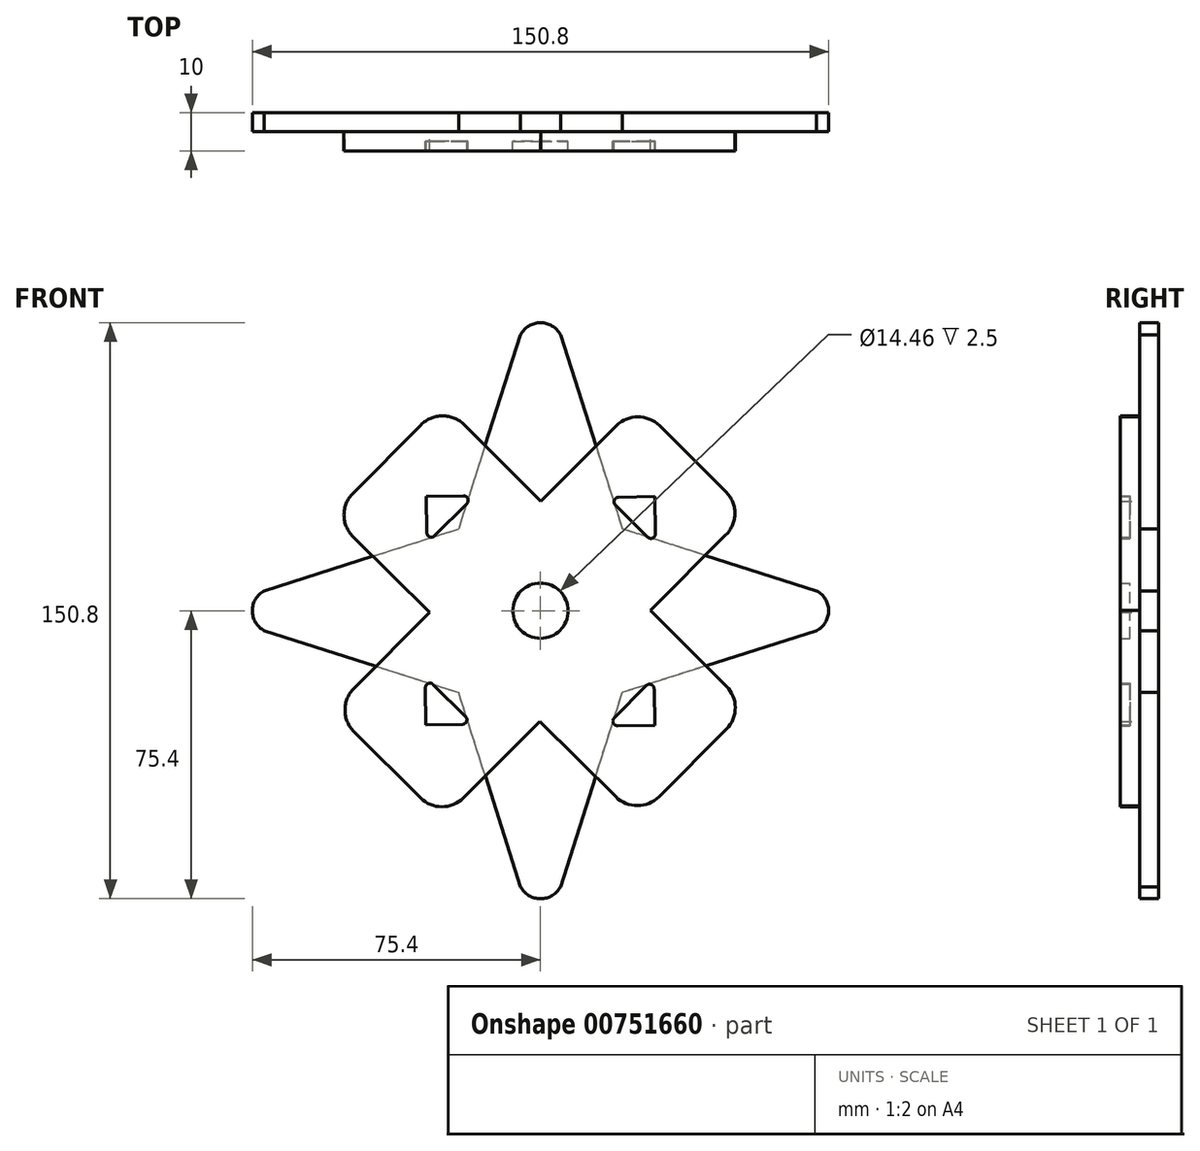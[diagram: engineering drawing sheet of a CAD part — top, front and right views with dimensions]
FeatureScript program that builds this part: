
annotation { "Feature Type Name" : "Feature", "Feature Type Description" : "" }
export const myFeature = defineFeature(function(context is Context, id is Id, definition is map)
    precondition{}
    {
        {
            var Q0;
            Q0=qCreatedBy(makeId("Front.planeOp"),FACE);
            var sketch = newSketch(context, id + "F0", { "sketchPlane" : qUnion([Q0])});
            skArc(sketch, "E0", {"start": v(5.71, 71.02) * mm, "mid": v(0.66, 75.37) * mm, "end": v(-5.23, 72.25) * mm});
            skLineSegment(sketch, "E1", {"start": v(-5.23, 72.25) * mm, "end": v(-21.41, 21.41) * mm});
            skLineSegment(sketch, "E2.MirrorCS", {"start": v(5.23, 72.25) * mm, "end": v(21.41, 21.41) * mm});
            skLineSegment(sketch, "E3", {"start": v(0, 75.37) * mm, "end": v(0, 0) * mm});
            skPoint(sketch, "E3.startSnap0", {"position": v(0.66, 75.37) * mm});
            skLineSegment(sketch, "E4.1.0", {"start": v(-75.37, 0) * mm, "end": v(0, 0) * mm});
            skArc(sketch, "E4.1.1", {"start": v(-71.02, 5.71) * mm, "mid": v(-75.37, 0.66) * mm, "end": v(-72.25, -5.23) * mm});
            skPoint(sketch, "E4.1.2", {"position": v(-75.37, 0.66) * mm});
            skLineSegment(sketch, "E4.1.3", {"start": v(-72.25, -5.23) * mm, "end": v(-21.41, -21.41) * mm});
            skLineSegment(sketch, "E4.1.4", {"start": v(-72.25, 5.23) * mm, "end": v(-21.41, 21.41) * mm});
            skLineSegment(sketch, "E4.2.0", {"start": v(0, -75.37) * mm, "end": v(0, 0) * mm});
            skArc(sketch, "E4.2.1", {"start": v(-5.71, -71.02) * mm, "mid": v(-0.66, -75.37) * mm, "end": v(5.23, -72.25) * mm});
            skPoint(sketch, "E4.2.2", {"position": v(-0.66, -75.37) * mm});
            skLineSegment(sketch, "E4.2.3", {"start": v(5.23, -72.25) * mm, "end": v(21.41, -21.41) * mm});
            skLineSegment(sketch, "E4.2.4", {"start": v(-5.23, -72.25) * mm, "end": v(-21.41, -21.41) * mm});
            skLineSegment(sketch, "E4.3.0", {"start": v(75.37, 0) * mm, "end": v(0, 0) * mm});
            skArc(sketch, "E4.3.1", {"start": v(71.02, -5.71) * mm, "mid": v(75.37, -0.66) * mm, "end": v(72.25, 5.23) * mm});
            skPoint(sketch, "E4.3.2", {"position": v(75.37, -0.66) * mm});
            skLineSegment(sketch, "E4.3.3", {"start": v(72.25, 5.23) * mm, "end": v(21.41, 21.41) * mm});
            skLineSegment(sketch, "E4.3.4", {"start": v(72.25, -5.23) * mm, "end": v(21.41, -21.41) * mm});
            skPoint(sketch, "E4.center", {"position": v(0, 0) * mm});
            skPoint(sketch, "E5.orphan", {"position": v(-18.17, 22.45) * mm});
            skPoint(sketch, "E6.orphan", {"position": v(-22.45, 18.17) * mm});
            skPoint(sketch, "E7.orphan", {"position": v(18.17, 22.45) * mm});
            skPoint(sketch, "E8.orphan", {"position": v(22.45, 18.17) * mm});
            skPoint(sketch, "E9.orphan", {"position": v(22.45, -18.17) * mm});
            skPoint(sketch, "E10.orphan", {"position": v(18.17, -22.45) * mm});
            skPoint(sketch, "E11.orphan", {"position": v(-18.17, -22.45) * mm});
            skPoint(sketch, "E12.orphan", {"position": v(-22.45, -18.17) * mm});
            skSolve(sketch);
        }
        {
            var Q0;
            Q0 = qSketchRegion(id + "F0", true);
            extrude(context, id + "F1", {"entities" : qUnion([Q0]), "oppositeDirection" : true, "depth" : 5 * mm, "offsetDistance" : 25 * mm});
        }
        {
            var Q0;
            Q0=qCreatedBy(makeId("Front.planeOp"),FACE);
            var sketch = newSketch(context, id + "F2", { "sketchPlane" : qUnion([Q0])});
            skLineSegment(sketch, "E13", {"start": v(-49.1, 30.74) * mm, "end": v(-31.28, 48.66) * mm});
            skLineSegment(sketch, "E14", {"start": v(-19.95, 48.69) * mm, "end": v(48.62, -19.7) * mm});
            skLineSegment(sketch, "E15", {"start": v(48.63, -31.01) * mm, "end": v(31, -48.68) * mm});
            skLineSegment(sketch, "E16", {"start": v(19.71, -48.72) * mm, "end": v(-49.05, 19.42) * mm});
            skPoint(sketch, "E17.visualSharp", {"position": v(-54.74, 25.05) * mm});
            skArc(sketch, "E17.filletArc", {"start": v(-49.1, 30.74) * mm, "mid": v(-51.42, 25.07) * mm, "end": v(-49.05, 19.42) * mm});
            skPoint(sketch, "E18.visualSharp", {"position": v(-25.63, 54.35) * mm});
            skArc(sketch, "E18.filletArc", {"start": v(-19.95, 48.69) * mm, "mid": v(-25.62, 51.02) * mm, "end": v(-31.28, 48.66) * mm});
            skPoint(sketch, "E19.visualSharp", {"position": v(25.38, -54.33) * mm});
            skArc(sketch, "E19.filletArc", {"start": v(19.71, -48.72) * mm, "mid": v(25.37, -51.04) * mm, "end": v(31, -48.68) * mm});
            skPoint(sketch, "E20.visualSharp", {"position": v(54.28, -25.35) * mm});
            skArc(sketch, "E20.filletArc", {"start": v(48.63, -31.01) * mm, "mid": v(50.97, -25.35) * mm, "end": v(48.62, -19.7) * mm});
            skLineSegment(sketch, "E21", {"start": v(31.15, 48.44) * mm, "end": v(48.5, 31.2) * mm});
            skLineSegment(sketch, "E22", {"start": v(48.53, 19.87) * mm, "end": v(-20.12, -48.96) * mm});
            skLineSegment(sketch, "E23", {"start": v(-31.43, -48.98) * mm, "end": v(-48.81, -31.64) * mm});
            skLineSegment(sketch, "E24", {"start": v(-48.82, -20.32) * mm, "end": v(19.85, 48.42) * mm});
            skPoint(sketch, "E25.visualSharp", {"position": v(25.49, 54.06) * mm});
            skArc(sketch, "E25.filletArc", {"start": v(31.15, 48.44) * mm, "mid": v(25.5, 50.76) * mm, "end": v(19.85, 48.42) * mm});
            skPoint(sketch, "E26.visualSharp", {"position": v(54.19, 25.55) * mm});
            skArc(sketch, "E26.filletArc", {"start": v(48.53, 19.87) * mm, "mid": v(50.86, 25.54) * mm, "end": v(48.5, 31.2) * mm});
            skPoint(sketch, "E27.visualSharp", {"position": v(-54.48, -25.99) * mm});
            skArc(sketch, "E27.filletArc", {"start": v(-48.82, -20.32) * mm, "mid": v(-51.16, -25.99) * mm, "end": v(-48.81, -31.64) * mm});
            skPoint(sketch, "E28.visualSharp", {"position": v(-25.77, -54.63) * mm});
            skArc(sketch, "E28.filletArc", {"start": v(-31.43, -48.98) * mm, "mid": v(-25.77, -51.31) * mm, "end": v(-20.12, -48.96) * mm});
            skSolve(sketch);
        }
        {
            var Q0;
            Q0 = qSketchRegion(id + "F2", true);
            extrude(context, id + "F3", {"entities" : qUnion([Q0]), "depth" : 5 * mm, "offsetDistance" : 25 * mm});
        }
        {
            var Q0;
            Q0=makeQuery(id+"F2.imprint","IMPRINT",FACE,{"disambiguationData":[TD([[makeQuery(id+"F2.imprint","IMPRINT",EDGE,{"derivedFrom":sQuery(id+"F2.wireOp",EDGE,"E21")}),-1.0]])]});
            var sketch = newSketch(context, id + "F4", { "sketchPlane" : qUnion([Q0])});
            skLineSegment(sketch, "E29", {"start": v(28.05, 19.28) * mm, "end": v(23.7, 23.62) * mm});
            skLineSegment(sketch, "E30", {"start": v(20.43, 29.73) * mm, "end": v(29.98, 29.94) * mm});
            skLineSegment(sketch, "E31", {"start": v(30.1, 20.15) * mm, "end": v(29.98, 29.94) * mm});
            skLineSegment(sketch, "E32", {"start": v(23.96, 23.36) * mm, "end": v(19.6, 27.68) * mm});
            skLineSegment(sketch, "E33", {"start": v(23.96, 23.36) * mm, "end": v(23.7, 23.62) * mm});
            skPoint(sketch, "E34.visualSharp", {"position": v(17.61, 29.67) * mm});
            skArc(sketch, "E34.filletArc", {"start": v(20.43, 29.73) * mm, "mid": v(19.34, 28.98) * mm, "end": v(19.6, 27.68) * mm});
            skPoint(sketch, "E35.visualSharp", {"position": v(30.13, 17.21) * mm});
            skArc(sketch, "E35.filletArc", {"start": v(28.05, 19.28) * mm, "mid": v(29.37, 19.03) * mm, "end": v(30.1, 20.15) * mm});
            skLineSegment(sketch, "E36.1.0", {"start": v(-23.36, 23.96) * mm, "end": v(-27.68, 19.6) * mm});
            skLineSegment(sketch, "E36.1.1", {"start": v(-20.15, 30.1) * mm, "end": v(-29.94, 29.98) * mm});
            skPoint(sketch, "E36.1.2", {"position": v(-17.21, 30.13) * mm});
            skLineSegment(sketch, "E36.1.3", {"start": v(-29.73, 20.43) * mm, "end": v(-29.94, 29.98) * mm});
            skPoint(sketch, "E36.1.4", {"position": v(-29.67, 17.61) * mm});
            skLineSegment(sketch, "E36.1.5", {"start": v(-19.28, 28.05) * mm, "end": v(-23.62, 23.7) * mm});
            skLineSegment(sketch, "E36.1.6", {"start": v(-23.36, 23.96) * mm, "end": v(-23.62, 23.7) * mm});
            skArc(sketch, "E36.1.7", {"start": v(-29.73, 20.43) * mm, "mid": v(-28.98, 19.34) * mm, "end": v(-27.68, 19.6) * mm});
            skArc(sketch, "E36.1.8", {"start": v(-19.28, 28.05) * mm, "mid": v(-19.03, 29.37) * mm, "end": v(-20.15, 30.1) * mm});
            skLineSegment(sketch, "E36.2.0", {"start": v(-23.96, -23.36) * mm, "end": v(-19.6, -27.68) * mm});
            skLineSegment(sketch, "E36.2.1", {"start": v(-30.1, -20.15) * mm, "end": v(-29.98, -29.94) * mm});
            skPoint(sketch, "E36.2.2", {"position": v(-30.13, -17.21) * mm});
            skLineSegment(sketch, "E36.2.3", {"start": v(-20.43, -29.73) * mm, "end": v(-29.98, -29.94) * mm});
            skPoint(sketch, "E36.2.4", {"position": v(-17.61, -29.67) * mm});
            skLineSegment(sketch, "E36.2.5", {"start": v(-28.05, -19.28) * mm, "end": v(-23.7, -23.62) * mm});
            skLineSegment(sketch, "E36.2.6", {"start": v(-23.96, -23.36) * mm, "end": v(-23.7, -23.62) * mm});
            skArc(sketch, "E36.2.7", {"start": v(-20.43, -29.73) * mm, "mid": v(-19.34, -28.98) * mm, "end": v(-19.6, -27.68) * mm});
            skArc(sketch, "E36.2.8", {"start": v(-28.05, -19.28) * mm, "mid": v(-29.37, -19.03) * mm, "end": v(-30.1, -20.15) * mm});
            skLineSegment(sketch, "E36.3.0", {"start": v(23.36, -23.96) * mm, "end": v(27.68, -19.6) * mm});
            skLineSegment(sketch, "E36.3.1", {"start": v(20.15, -30.1) * mm, "end": v(29.94, -29.98) * mm});
            skPoint(sketch, "E36.3.2", {"position": v(17.21, -30.13) * mm});
            skLineSegment(sketch, "E36.3.3", {"start": v(29.73, -20.43) * mm, "end": v(29.94, -29.98) * mm});
            skPoint(sketch, "E36.3.4", {"position": v(29.67, -17.61) * mm});
            skLineSegment(sketch, "E36.3.5", {"start": v(19.28, -28.05) * mm, "end": v(23.62, -23.7) * mm});
            skLineSegment(sketch, "E36.3.6", {"start": v(23.36, -23.96) * mm, "end": v(23.62, -23.7) * mm});
            skArc(sketch, "E36.3.7", {"start": v(29.73, -20.43) * mm, "mid": v(28.98, -19.34) * mm, "end": v(27.68, -19.6) * mm});
            skArc(sketch, "E36.3.8", {"start": v(19.28, -28.05) * mm, "mid": v(19.03, -29.37) * mm, "end": v(20.15, -30.1) * mm});
            skPoint(sketch, "E36.center", {"position": v(0, 0) * mm});
            skSolve(sketch);
        }
        {
            var Q0;
            Q0 = qSketchRegion(id + "F4", true);
            extrude(context, id + "F5", {"entities" : qUnion([Q0]), "operationType" : NewBodyOperationType.REMOVE, "depth" : 11 * mm, "offsetDistance" : 25 * mm, "hasSecondDirection" : true, "secondDirectionOppositeDirection" : false, "secondDirectionDepth" : 2.5 * mm});
        }
        {
            var Q0;
            Q0=qCreatedBy(makeId("Front.planeOp"),FACE);
            var sketch = newSketch(context, id + "F6", { "sketchPlane" : qUnion([Q0])});
            skCircle(sketch, "E37", {"center": v(0, 0) * mm, "radius": 7.23 * mm});
            skSolve(sketch);
        }
        {
            var Q0;
            Q0 = qSketchRegion(id + "F6", true);
            extrude(context, id + "F7", {"entities" : qUnion([Q0]), "operationType" : NewBodyOperationType.REMOVE, "depth" : 11 * mm, "offsetDistance" : 25 * mm, "hasSecondDirection" : true, "secondDirectionOppositeDirection" : false, "secondDirectionDepth" : 2.5 * mm});
        }
    });
